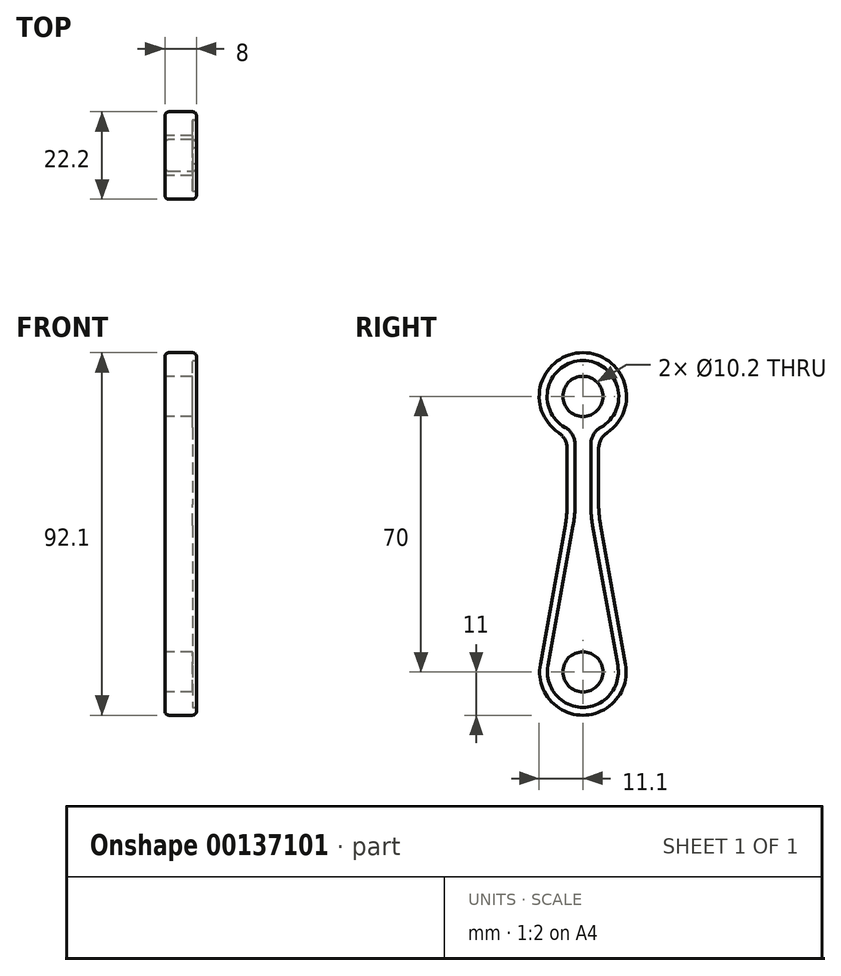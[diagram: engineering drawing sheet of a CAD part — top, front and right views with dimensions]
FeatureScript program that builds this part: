
annotation { "Feature Type Name" : "Feature", "Feature Type Description" : "" }
export const myFeature = defineFeature(function(context is Context, id is Id, definition is map)
    precondition{}
    {
        {
            var Q0;
            Q0=qCreatedBy(makeId("Right.planeOp"),FACE);
            var sketch = newSketch(context, id + "F0", { "sketchPlane" : qUnion([Q0])});
            skCircle(sketch, "E0", {"center": v(0, 0) * mm, "radius": 5.1 * mm});
            skCircle(sketch, "E1", {"center": v(0, 0) * mm, "radius": 11.1 * mm});
            skCircle(sketch, "E2", {"center": v(0, -70) * mm, "radius": 5.1 * mm});
            skCircle(sketch, "E3", {"center": v(0, -70) * mm, "radius": 11 * mm});
            skLineSegment(sketch, "E4", {"start": v(-4, -10.35) * mm, "end": v(-4, -30) * mm});
            skLineSegment(sketch, "E5", {"start": v(-4, -30) * mm, "end": v(-10.83, -68.06) * mm});
            skLineSegment(sketch, "E6", {"start": v(4, -10.35) * mm, "end": v(4, -30) * mm});
            skLineSegment(sketch, "E7", {"start": v(4, -30) * mm, "end": v(10.83, -68.06) * mm});
            skSolve(sketch);
        }
        {
            var Q0;
            Q0=makeQuery(id+"F0.imprint","IMPRINT",FACE,{"disambiguationData":[TD([[makeQuery(id+"F0.imprint","IMPRINT",EDGE,{"derivedFrom":sQuery(id+"F0.wireOp",EDGE,"E0")}),-1.0]])]});
            var Q1;
            {var subQ1=sQuery(id+"F0.wireOp",EDGE,"E4");Q1=makeQuery(id+"F0.imprint","IMPRINT",FACE,{"disambiguationData":[TD([[makeQuery(id+"F0.imprint","IMPRINT",EDGE,{"derivedFrom":subQ1}),1.0]])]});}
            var Q2;
            Q2=makeQuery(id+"F0.imprint","IMPRINT",FACE,{"disambiguationData":[TD([[makeQuery(id+"F0.imprint","IMPRINT",EDGE,{"derivedFrom":sQuery(id+"F0.wireOp",EDGE,"E2")}),-1.0]])]});
            extrude(context, id + "F1", {"entities" : qUnion([Q0, Q1, Q2]), "endBound" : BoundingType.SYMMETRIC, "depth" : 8 * mm});
        }
        {
            var Q0;
            Q0=makeQuery(id+"F1.opExtrude","CAP_FACE",FACE,{"disambiguationData":[OSD([sQuery(id+"F0.wireOp",EDGE,"E0"),sQuery(id+"F0.wireOp",EDGE,"E1"),sQuery(id+"F0.wireOp",EDGE,"E2"),sQuery(id+"F0.wireOp",EDGE,"E3"),sQuery(id+"F0.wireOp",EDGE,"E4"),sQuery(id+"F0.wireOp",EDGE,"E5"),sQuery(id+"F0.wireOp",EDGE,"E6"),sQuery(id+"F0.wireOp",EDGE,"E7")])],"isStart":false});
            var sketch = newSketch(context, id + "F2", { "sketchPlane" : qUnion([Q0])});
            skLineSegment(sketch, "E8.0", {"start": v(2, -8.88) * mm, "end": v(2, -30.18) * mm});
            skLineSegment(sketch, "E8.1", {"start": v(-2, -8.88) * mm, "end": v(-2, -30.18) * mm});
            skArc(sketch, "E8.3", {"start": v(2, -8.88) * mm, "mid": v(0, 9.1) * mm, "end": v(-2, -8.88) * mm});
            skLineSegment(sketch, "E9.0", {"start": v(2, -30.18) * mm, "end": v(8.86, -68.41) * mm});
            skArc(sketch, "E9.1", {"start": v(-8.86, -68.41) * mm, "mid": v(0, -79) * mm, "end": v(8.86, -68.41) * mm});
            skLineSegment(sketch, "E9.2", {"start": v(-2, -30.18) * mm, "end": v(-8.86, -68.41) * mm});
            skSolve(sketch);
        }
        {
            var Q0;
            Q0=makeQuery(id+"F2.imprint","IMPRINT",FACE,{"disambiguationData":[TD([[makeQuery(id+"F2.imprint","IMPRINT",EDGE,{"derivedFrom":sQuery(id+"F2.wireOp",EDGE,"E8.0")}),-1.0]])]});
            extrude(context, id + "F3", {"entities" : qUnion([Q0]), "operationType" : NewBodyOperationType.REMOVE, "oppositeDirection" : true, "depth" : 1 * mm});
        }
        {
            var Q0;
            Q0=makeQuery(id+"F1.opExtrude","SWEPT_EDGE",EDGE,{"disambiguationData":[OSD([sQuery(id+"F0.wireOp",EDGE,"E4"),sQuery(id+"F0.wireOp",EDGE,"E5")])]});
            var Q1;
            Q1=makeQuery(id+"F1.opExtrude","SWEPT_EDGE",EDGE,{"disambiguationData":[OSD([sQuery(id+"F0.wireOp",EDGE,"E6"),sQuery(id+"F0.wireOp",EDGE,"E7")])]});
            fillet(context, id + "F4", {"entities" : qUnion([Q0, Q1]), "radius" : 30 * mm, "tangentPropagation" : true, "allowEdgeOverflow" : false});
        }
        {
            var Q0;
            Q0=makeQuery(id+"F1.opExtrude","SWEPT_EDGE",EDGE,{"disambiguationData":[OSD([sQuery(id+"F0.wireOp",EDGE,"E1"),sQuery(id+"F0.wireOp",EDGE,"E4")])]});
            var Q1;
            Q1=makeQuery(id+"F1.opExtrude","SWEPT_EDGE",EDGE,{"disambiguationData":[OSD([sQuery(id+"F0.wireOp",EDGE,"E1"),sQuery(id+"F0.wireOp",EDGE,"E6")])]});
            fillet(context, id + "F5", {"entities" : qUnion([Q0, Q1]), "radius" : 5 * mm, "tangentPropagation" : true, "allowEdgeOverflow" : false});
        }
        {
            var Q0;
            Q0=makeQuery(id+"F3.boolean.opBoolean","COPY",EDGE,{"derivedFrom":makeQuery(id+"F3.opExtrude","SWEPT_EDGE",EDGE,{"disambiguationData":[OSD([sQuery(id+"F2.wireOp",EDGE,"E8.1"),sQuery(id+"F2.wireOp",EDGE,"E8.3")])]})});
            var Q1;
            Q1=makeQuery(id+"F3.boolean.opBoolean","COPY",EDGE,{"derivedFrom":makeQuery(id+"F3.opExtrude","SWEPT_EDGE",EDGE,{"disambiguationData":[OSD([sQuery(id+"F2.wireOp",EDGE,"E8.0"),sQuery(id+"F2.wireOp",EDGE,"E8.3")])]})});
            fillet(context, id + "F6", {"entities" : qUnion([Q0, Q1]), "radius" : 5 * mm, "tangentPropagation" : true, "allowEdgeOverflow" : false});
        }
        {
            var Q0;
            Q0=makeQuery(id+"F3.boolean.opBoolean","COPY",EDGE,{"derivedFrom":makeQuery(id+"F3.opExtrude","SWEPT_EDGE",EDGE,{"disambiguationData":[OSD([sQuery(id+"F2.wireOp",EDGE,"E8.1"),sQuery(id+"F2.wireOp",EDGE,"E8.2")])]})});
            var Q1;
            Q1=makeQuery(id+"F3.boolean.opBoolean","COPY",EDGE,{"derivedFrom":makeQuery(id+"F3.opExtrude","SWEPT_EDGE",EDGE,{"disambiguationData":[OSD([sQuery(id+"F2.wireOp",EDGE,"E8.0"),sQuery(id+"F2.wireOp",EDGE,"E8.5")])]})});
            fillet(context, id + "F7", {"entities" : qUnion([Q0, Q1]), "radius" : 30 * mm, "tangentPropagation" : true, "allowEdgeOverflow" : false});
        }
        {
            var Q0;
            Q0=makeQuery(id+"F1.opExtrude","CAP_EDGE",EDGE,{"disambiguationData":[OSD([sQuery(id+"F0.wireOp",EDGE,"E1")])],"isStart":false});
            var Q1;
            {var subQ0=sQuery(id+"F0.wireOp",EDGE,"E4");var subQ1=sQuery(id+"F0.wireOp",EDGE,"E1");Q1=makeQuery(id+"F5.opFillet","BLEND_EDGE",EDGE,{"blendedFrom":[makeQuery(id+"F1.opExtrude","SWEPT_EDGE",EDGE,{"disambiguationData":[OSD([subQ1,subQ0])]}),makeQuery(id+"F1.opExtrude","CAP_FACE",FACE,{"disambiguationData":[OSD([sQuery(id+"F0.wireOp",EDGE,"E0"),subQ1,sQuery(id+"F0.wireOp",EDGE,"E2"),sQuery(id+"F0.wireOp",EDGE,"E3"),subQ0,sQuery(id+"F0.wireOp",EDGE,"E5"),sQuery(id+"F0.wireOp",EDGE,"E6"),sQuery(id+"F0.wireOp",EDGE,"E7")])],"isStart":false})],"blendedInto":[makeQuery(id+"F1.opExtrude","CAP_FACE",FACE,{"disambiguationData":[OSD([sQuery(id+"F0.wireOp",EDGE,"E0"),subQ1,sQuery(id+"F0.wireOp",EDGE,"E2"),sQuery(id+"F0.wireOp",EDGE,"E3"),subQ0,sQuery(id+"F0.wireOp",EDGE,"E5"),sQuery(id+"F0.wireOp",EDGE,"E6"),sQuery(id+"F0.wireOp",EDGE,"E7")])],"isStart":false})]});}
            var Q2;
            Q2=makeQuery(id+"F1.opExtrude","CAP_EDGE",EDGE,{"disambiguationData":[OSD([sQuery(id+"F0.wireOp",EDGE,"E4")])],"isStart":false});
            var Q3;
            {var subQ0=sQuery(id+"F0.wireOp",EDGE,"E5");var subQ1=sQuery(id+"F0.wireOp",EDGE,"E4");Q3=makeQuery(id+"F4.opFillet","BLEND_EDGE",EDGE,{"blendedFrom":[makeQuery(id+"F1.opExtrude","SWEPT_EDGE",EDGE,{"disambiguationData":[OSD([subQ1,subQ0])]}),makeQuery(id+"F1.opExtrude","CAP_FACE",FACE,{"disambiguationData":[OSD([sQuery(id+"F0.wireOp",EDGE,"E0"),sQuery(id+"F0.wireOp",EDGE,"E1"),sQuery(id+"F0.wireOp",EDGE,"E2"),sQuery(id+"F0.wireOp",EDGE,"E3"),subQ1,subQ0,sQuery(id+"F0.wireOp",EDGE,"E6"),sQuery(id+"F0.wireOp",EDGE,"E7")])],"isStart":false})],"blendedInto":[makeQuery(id+"F1.opExtrude","CAP_FACE",FACE,{"disambiguationData":[OSD([sQuery(id+"F0.wireOp",EDGE,"E0"),sQuery(id+"F0.wireOp",EDGE,"E1"),sQuery(id+"F0.wireOp",EDGE,"E2"),sQuery(id+"F0.wireOp",EDGE,"E3"),subQ1,subQ0,sQuery(id+"F0.wireOp",EDGE,"E6"),sQuery(id+"F0.wireOp",EDGE,"E7")])],"isStart":false})]});}
            var Q4;
            Q4=makeQuery(id+"F1.opExtrude","CAP_EDGE",EDGE,{"disambiguationData":[OSD([sQuery(id+"F0.wireOp",EDGE,"E5")])],"isStart":false});
            var Q5;
            Q5=makeQuery(id+"F1.opExtrude","CAP_EDGE",EDGE,{"disambiguationData":[OSD([sQuery(id+"F0.wireOp",EDGE,"E3")])],"isStart":false});
            var Q6;
            Q6=makeQuery(id+"F1.opExtrude","CAP_EDGE",EDGE,{"disambiguationData":[OSD([sQuery(id+"F0.wireOp",EDGE,"E7")])],"isStart":false});
            var Q7;
            {var subQ0=sQuery(id+"F0.wireOp",EDGE,"E7");var subQ1=sQuery(id+"F0.wireOp",EDGE,"E6");Q7=makeQuery(id+"F4.opFillet","BLEND_EDGE",EDGE,{"blendedFrom":[makeQuery(id+"F1.opExtrude","SWEPT_EDGE",EDGE,{"disambiguationData":[OSD([subQ1,subQ0])]}),makeQuery(id+"F1.opExtrude","CAP_FACE",FACE,{"disambiguationData":[OSD([sQuery(id+"F0.wireOp",EDGE,"E0"),sQuery(id+"F0.wireOp",EDGE,"E1"),sQuery(id+"F0.wireOp",EDGE,"E2"),sQuery(id+"F0.wireOp",EDGE,"E3"),sQuery(id+"F0.wireOp",EDGE,"E4"),sQuery(id+"F0.wireOp",EDGE,"E5"),subQ1,subQ0])],"isStart":false})],"blendedInto":[makeQuery(id+"F1.opExtrude","CAP_FACE",FACE,{"disambiguationData":[OSD([sQuery(id+"F0.wireOp",EDGE,"E0"),sQuery(id+"F0.wireOp",EDGE,"E1"),sQuery(id+"F0.wireOp",EDGE,"E2"),sQuery(id+"F0.wireOp",EDGE,"E3"),sQuery(id+"F0.wireOp",EDGE,"E4"),sQuery(id+"F0.wireOp",EDGE,"E5"),subQ1,subQ0])],"isStart":false})]});}
            var Q8;
            Q8=makeQuery(id+"F1.opExtrude","CAP_EDGE",EDGE,{"disambiguationData":[OSD([sQuery(id+"F0.wireOp",EDGE,"E6")])],"isStart":false});
            var Q9;
            {var subQ0=sQuery(id+"F0.wireOp",EDGE,"E6");var subQ1=sQuery(id+"F0.wireOp",EDGE,"E1");Q9=makeQuery(id+"F5.opFillet","BLEND_EDGE",EDGE,{"blendedFrom":[makeQuery(id+"F1.opExtrude","SWEPT_EDGE",EDGE,{"disambiguationData":[OSD([subQ1,subQ0])]}),makeQuery(id+"F1.opExtrude","CAP_FACE",FACE,{"disambiguationData":[OSD([sQuery(id+"F0.wireOp",EDGE,"E0"),subQ1,sQuery(id+"F0.wireOp",EDGE,"E2"),sQuery(id+"F0.wireOp",EDGE,"E3"),sQuery(id+"F0.wireOp",EDGE,"E4"),sQuery(id+"F0.wireOp",EDGE,"E5"),subQ0,sQuery(id+"F0.wireOp",EDGE,"E7")])],"isStart":false})],"blendedInto":[makeQuery(id+"F1.opExtrude","CAP_FACE",FACE,{"disambiguationData":[OSD([sQuery(id+"F0.wireOp",EDGE,"E0"),subQ1,sQuery(id+"F0.wireOp",EDGE,"E2"),sQuery(id+"F0.wireOp",EDGE,"E3"),sQuery(id+"F0.wireOp",EDGE,"E4"),sQuery(id+"F0.wireOp",EDGE,"E5"),subQ0,sQuery(id+"F0.wireOp",EDGE,"E7")])],"isStart":false})]});}
            fillet(context, id + "F8", {"entities" : qUnion([Q0, Q1, Q2, Q3, Q4, Q5, Q6, Q7, Q8, Q9]), "radius" : 1 * mm, "tangentPropagation" : true, "allowEdgeOverflow" : false});
        }
        {
            var Q0;
            Q0=makeQuery(id+"F1.opExtrude","CAP_EDGE",EDGE,{"disambiguationData":[OSD([sQuery(id+"F0.wireOp",EDGE,"E1")])],"isStart":true});
            var Q1;
            {var subQ0=sQuery(id+"F0.wireOp",EDGE,"E4");var subQ1=sQuery(id+"F0.wireOp",EDGE,"E1");Q1=makeQuery(id+"F5.opFillet","BLEND_EDGE",EDGE,{"blendedFrom":[makeQuery(id+"F1.opExtrude","SWEPT_EDGE",EDGE,{"disambiguationData":[OSD([subQ1,subQ0])]}),makeQuery(id+"F1.opExtrude","CAP_FACE",FACE,{"disambiguationData":[OSD([sQuery(id+"F0.wireOp",EDGE,"E0"),subQ1,sQuery(id+"F0.wireOp",EDGE,"E2"),sQuery(id+"F0.wireOp",EDGE,"E3"),subQ0,sQuery(id+"F0.wireOp",EDGE,"E5"),sQuery(id+"F0.wireOp",EDGE,"E6"),sQuery(id+"F0.wireOp",EDGE,"E7")])],"isStart":true})],"blendedInto":[makeQuery(id+"F1.opExtrude","CAP_FACE",FACE,{"disambiguationData":[OSD([sQuery(id+"F0.wireOp",EDGE,"E0"),subQ1,sQuery(id+"F0.wireOp",EDGE,"E2"),sQuery(id+"F0.wireOp",EDGE,"E3"),subQ0,sQuery(id+"F0.wireOp",EDGE,"E5"),sQuery(id+"F0.wireOp",EDGE,"E6"),sQuery(id+"F0.wireOp",EDGE,"E7")])],"isStart":true})]});}
            var Q2;
            {var subQ0=sQuery(id+"F0.wireOp",EDGE,"E6");var subQ1=sQuery(id+"F0.wireOp",EDGE,"E1");Q2=makeQuery(id+"F5.opFillet","BLEND_EDGE",EDGE,{"blendedFrom":[makeQuery(id+"F1.opExtrude","SWEPT_EDGE",EDGE,{"disambiguationData":[OSD([subQ1,subQ0])]}),makeQuery(id+"F1.opExtrude","CAP_FACE",FACE,{"disambiguationData":[OSD([sQuery(id+"F0.wireOp",EDGE,"E0"),subQ1,sQuery(id+"F0.wireOp",EDGE,"E2"),sQuery(id+"F0.wireOp",EDGE,"E3"),sQuery(id+"F0.wireOp",EDGE,"E4"),sQuery(id+"F0.wireOp",EDGE,"E5"),subQ0,sQuery(id+"F0.wireOp",EDGE,"E7")])],"isStart":true})],"blendedInto":[makeQuery(id+"F1.opExtrude","CAP_FACE",FACE,{"disambiguationData":[OSD([sQuery(id+"F0.wireOp",EDGE,"E0"),subQ1,sQuery(id+"F0.wireOp",EDGE,"E2"),sQuery(id+"F0.wireOp",EDGE,"E3"),sQuery(id+"F0.wireOp",EDGE,"E4"),sQuery(id+"F0.wireOp",EDGE,"E5"),subQ0,sQuery(id+"F0.wireOp",EDGE,"E7")])],"isStart":true})]});}
            var Q3;
            Q3=makeQuery(id+"F1.opExtrude","CAP_EDGE",EDGE,{"disambiguationData":[OSD([sQuery(id+"F0.wireOp",EDGE,"E6")])],"isStart":true});
            var Q4;
            Q4=makeQuery(id+"F1.opExtrude","CAP_EDGE",EDGE,{"disambiguationData":[OSD([sQuery(id+"F0.wireOp",EDGE,"E4")])],"isStart":true});
            var Q5;
            {var subQ0=sQuery(id+"F0.wireOp",EDGE,"E5");var subQ1=sQuery(id+"F0.wireOp",EDGE,"E4");Q5=makeQuery(id+"F4.opFillet","BLEND_EDGE",EDGE,{"blendedFrom":[makeQuery(id+"F1.opExtrude","SWEPT_EDGE",EDGE,{"disambiguationData":[OSD([subQ1,subQ0])]}),makeQuery(id+"F1.opExtrude","CAP_FACE",FACE,{"disambiguationData":[OSD([sQuery(id+"F0.wireOp",EDGE,"E0"),sQuery(id+"F0.wireOp",EDGE,"E1"),sQuery(id+"F0.wireOp",EDGE,"E2"),sQuery(id+"F0.wireOp",EDGE,"E3"),subQ1,subQ0,sQuery(id+"F0.wireOp",EDGE,"E6"),sQuery(id+"F0.wireOp",EDGE,"E7")])],"isStart":true})],"blendedInto":[makeQuery(id+"F1.opExtrude","CAP_FACE",FACE,{"disambiguationData":[OSD([sQuery(id+"F0.wireOp",EDGE,"E0"),sQuery(id+"F0.wireOp",EDGE,"E1"),sQuery(id+"F0.wireOp",EDGE,"E2"),sQuery(id+"F0.wireOp",EDGE,"E3"),subQ1,subQ0,sQuery(id+"F0.wireOp",EDGE,"E6"),sQuery(id+"F0.wireOp",EDGE,"E7")])],"isStart":true})]});}
            var Q6;
            Q6=makeQuery(id+"F1.opExtrude","CAP_EDGE",EDGE,{"disambiguationData":[OSD([sQuery(id+"F0.wireOp",EDGE,"E5")])],"isStart":true});
            var Q7;
            Q7=makeQuery(id+"F1.opExtrude","CAP_EDGE",EDGE,{"disambiguationData":[OSD([sQuery(id+"F0.wireOp",EDGE,"E3")])],"isStart":true});
            var Q8;
            Q8=makeQuery(id+"F1.opExtrude","CAP_EDGE",EDGE,{"disambiguationData":[OSD([sQuery(id+"F0.wireOp",EDGE,"E7")])],"isStart":true});
            var Q9;
            {var subQ0=sQuery(id+"F0.wireOp",EDGE,"E7");var subQ1=sQuery(id+"F0.wireOp",EDGE,"E6");Q9=makeQuery(id+"F4.opFillet","BLEND_EDGE",EDGE,{"blendedFrom":[makeQuery(id+"F1.opExtrude","SWEPT_EDGE",EDGE,{"disambiguationData":[OSD([subQ1,subQ0])]}),makeQuery(id+"F1.opExtrude","CAP_FACE",FACE,{"disambiguationData":[OSD([sQuery(id+"F0.wireOp",EDGE,"E0"),sQuery(id+"F0.wireOp",EDGE,"E1"),sQuery(id+"F0.wireOp",EDGE,"E2"),sQuery(id+"F0.wireOp",EDGE,"E3"),sQuery(id+"F0.wireOp",EDGE,"E4"),sQuery(id+"F0.wireOp",EDGE,"E5"),subQ1,subQ0])],"isStart":true})],"blendedInto":[makeQuery(id+"F1.opExtrude","CAP_FACE",FACE,{"disambiguationData":[OSD([sQuery(id+"F0.wireOp",EDGE,"E0"),sQuery(id+"F0.wireOp",EDGE,"E1"),sQuery(id+"F0.wireOp",EDGE,"E2"),sQuery(id+"F0.wireOp",EDGE,"E3"),sQuery(id+"F0.wireOp",EDGE,"E4"),sQuery(id+"F0.wireOp",EDGE,"E5"),subQ1,subQ0])],"isStart":true})]});}
            fillet(context, id + "F9", {"entities" : qUnion([Q0, Q1, Q2, Q3, Q4, Q5, Q6, Q7, Q8, Q9]), "radius" : 1 * mm, "tangentPropagation" : true, "allowEdgeOverflow" : false});
        }
    });
